# Revit family: B_1
name_source: partatom
category: Specialty Equipment
units: mm (PartAtom-declared; Revit-internal decimal feet)

## family parameters
Cut with Voids When Loaded = No
Host = Face
OmniClass Number = 23.31.25.00
Part Type = Normal
Room Calculation Point = No
Round Connector Dimension = Use Diameter
Shared = No

## types (1)
- NA-Black
    ADA Compliant = No
    Assembly Code = C1030200
    Date Modified = 05/08/2024
    Default Elevation = 42"
    Description = Sink Cover
    Finish = KOHLER-Paper_Composite-NA-Black
    Height = 3/8"
    Length = 21 7/8"
    Manufacturer = Kohler Co.
    Master Format 2014 = 10 28 00
    Master Format 2014 Name = Toilet, Bath, and Laundry Accessories
    Material = Paper Composite Construction
    Model = K-35003-NA
    Product Documentation Link = https://www.us.kohler.com
    Product Name = Bevel
    Product Page URL = http://www.us.kohler.com
    Type = 1
    URL = https://www.us.kohler.com
    WaterSense Certified = No
    Width = 17 7/16"

## geometry (parser evidence)
native form markers: Sweep x5
no freeform markers — native parametric forms only
